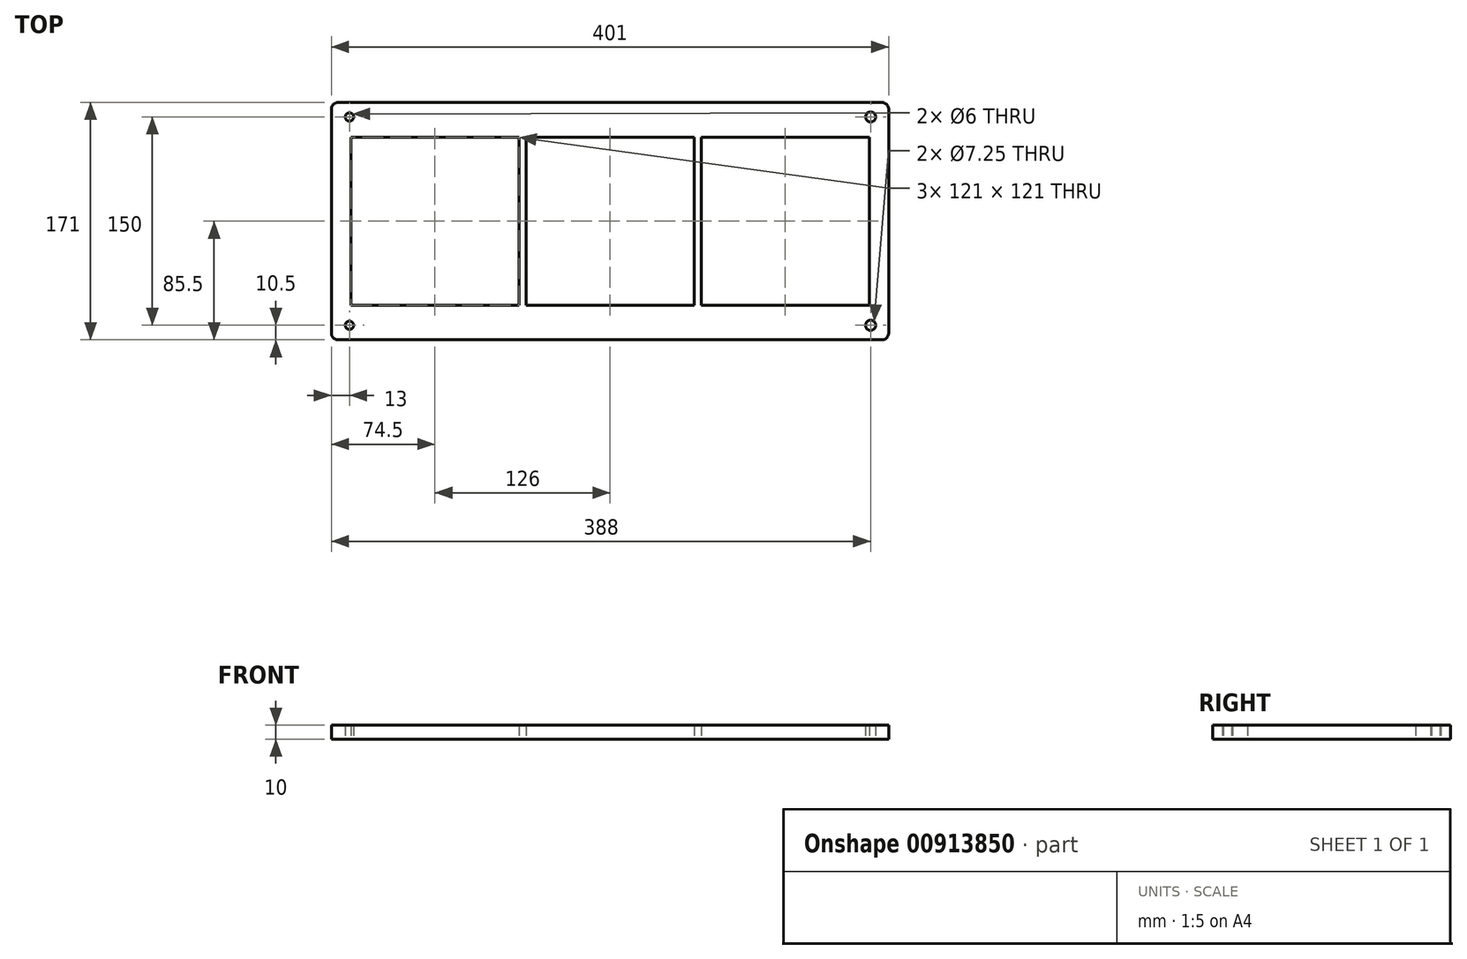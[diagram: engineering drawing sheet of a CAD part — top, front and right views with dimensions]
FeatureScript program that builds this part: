
annotation { "Feature Type Name" : "Feature", "Feature Type Description" : "" }
export const myFeature = defineFeature(function(context is Context, id is Id, definition is map)
    precondition{}
    {
        {
            var Q0;
            Q0=qCreatedBy(makeId("Top.planeOp"),FACE);
            var sketch = newSketch(context, id + "F0", { "sketchPlane" : qUnion([Q0])});
            skLineSegment(sketch, "E0.bottom", {"start": v(0, 0) * mm, "end": v(121, 0) * mm});
            skLineSegment(sketch, "E0.top", {"start": v(0, -121) * mm, "end": v(121, -121) * mm});
            skLineSegment(sketch, "E0.left", {"start": v(0, 0) * mm, "end": v(0, -121) * mm});
            skLineSegment(sketch, "E0.right", {"start": v(121, 0) * mm, "end": v(121, -121) * mm});
            skLineSegment(sketch, "E1.bottom", {"start": v(-140, 25) * mm, "end": v(261, 25) * mm});
            skLineSegment(sketch, "E1.top", {"start": v(-140, -146) * mm, "end": v(261, -146) * mm});
            skLineSegment(sketch, "E1.left", {"start": v(-140, 25) * mm, "end": v(-140, -146) * mm});
            skLineSegment(sketch, "E1.right", {"start": v(261, 25) * mm, "end": v(261, -146) * mm});
            skCircle(sketch, "E2", {"center": v(-127, 14.5) * mm, "radius": 3 * mm});
            skCircle(sketch, "E3", {"center": v(248, 14.5) * mm, "radius": 3.63 * mm});
            skCircle(sketch, "E4", {"center": v(-127, -135.5) * mm, "radius": 3 * mm});
            skCircle(sketch, "E5", {"center": v(248, -135.5) * mm, "radius": 3.63 * mm});
            skLineSegment(sketch, "E6", {"start": v(-127, -135.5) * mm, "end": v(-127, 14.5) * mm, "construction": true});
            skPoint(sketch, "E7", {"position": v(-140, -60.5) * mm});
            skPoint(sketch, "E8", {"position": v(-127, -60.5) * mm});
            skPoint(sketch, "E8.positionSnap0", {"position": v(-127, -60.5) * mm});
            skLineSegment(sketch, "E9", {"start": v(-127, -135.5) * mm, "end": v(248, -135.5) * mm, "construction": true});
            skPoint(sketch, "E10", {"position": v(60.5, -135.5) * mm});
            skPoint(sketch, "E11", {"position": v(60.5, -146) * mm});
            skLineSegment(sketch, "E12.bottom", {"start": v(-5, 0) * mm, "end": v(-126, 0) * mm});
            skLineSegment(sketch, "E12.top", {"start": v(-5, -121) * mm, "end": v(-126, -121) * mm});
            skLineSegment(sketch, "E12.left", {"start": v(-5, 0) * mm, "end": v(-5, -121) * mm});
            skLineSegment(sketch, "E12.right", {"start": v(-126, 0) * mm, "end": v(-126, -121) * mm});
            skLineSegment(sketch, "E13.bottom", {"start": v(126, 0) * mm, "end": v(247, 0) * mm});
            skLineSegment(sketch, "E13.top", {"start": v(126, -121) * mm, "end": v(247, -121) * mm});
            skLineSegment(sketch, "E13.left", {"start": v(126, 0) * mm, "end": v(126, -121) * mm});
            skLineSegment(sketch, "E13.right", {"start": v(247, 0) * mm, "end": v(247, -121) * mm});
            skPoint(sketch, "E14", {"position": v(60.5, -121) * mm});
            skSolve(sketch);
        }
        {
            var Q0;
            Q0 = qSketchRegion(id + "F0", true);
            extrude(context, id + "F1", {"entities" : qUnion([Q0]), "depth" : 10 * mm, "offsetDistance" : 25 * mm});
        }
        {
            var Q0;
            Q0=makeQuery(id+"F1.opExtrude","SWEPT_EDGE",EDGE,{"disambiguationData":[OSD([sQuery(id+"F0.wireOp",EDGE,"E1.bottom"),sQuery(id+"F0.wireOp",EDGE,"E1.right")])]});
            var Q1;
            Q1=makeQuery(id+"F1.opExtrude","SWEPT_EDGE",EDGE,{"disambiguationData":[OSD([sQuery(id+"F0.wireOp",EDGE,"E1.top"),sQuery(id+"F0.wireOp",EDGE,"E1.right")])]});
            var Q2;
            Q2=makeQuery(id+"F1.opExtrude","SWEPT_EDGE",EDGE,{"disambiguationData":[OSD([sQuery(id+"F0.wireOp",EDGE,"E1.top"),sQuery(id+"F0.wireOp",EDGE,"E1.left")])]});
            var Q3;
            Q3=makeQuery(id+"F1.opExtrude","SWEPT_EDGE",EDGE,{"disambiguationData":[OSD([sQuery(id+"F0.wireOp",EDGE,"E1.bottom"),sQuery(id+"F0.wireOp",EDGE,"E1.left")])]});
            fillet(context, id + "F2", {"entities" : qUnion([Q0, Q1, Q2, Q3]), "tangentPropagation" : true, "radius" : 5 * mm, "defaultsChanged" : false, "vertexSettings" : [], "allowEdgeOverflow" : false});
        }
    });
